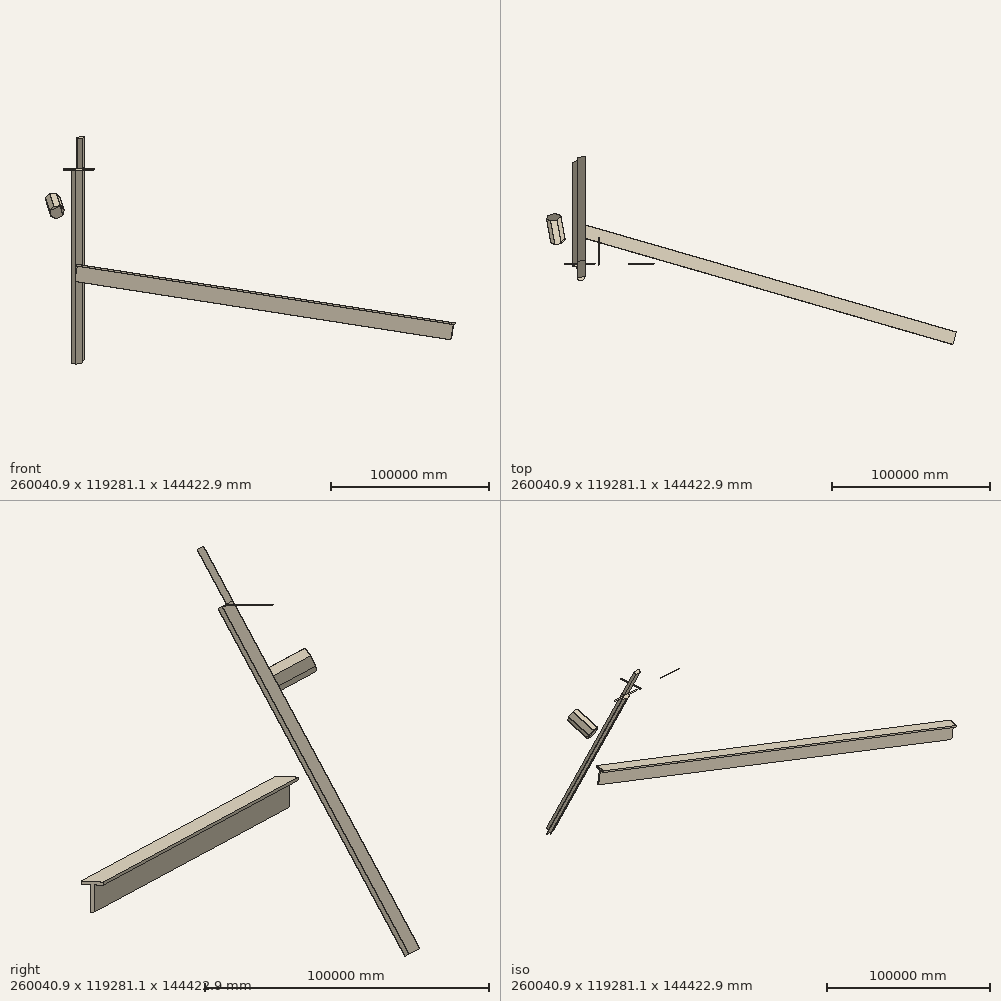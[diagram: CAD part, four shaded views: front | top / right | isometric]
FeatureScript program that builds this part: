
annotation { "Feature Type Name" : "Feature", "Feature Type Description" : "" }
export const myFeature = defineFeature(function(context is Context, id is Id, definition is map)
    precondition{}
    {
        {
            var Q0;
            Q0=qCreatedBy(makeId("Right.planeOp"),FACE);
            var sketch = newSketch(context, id + "F0", { "sketchPlane" : qUnion([Q0])});
            skLineSegment(sketch, "E0", {"start": v(0, 0) * mm, "end": v(0, 75.63) * mm});
            skLineSegment(sketch, "E1", {"start": v(76.11, 75.63) * mm, "end": v(76.11, 0) * mm});
            skLineSegment(sketch, "E2", {"start": v(76.11, 0) * mm, "end": v(0, 0) * mm});
            skLineSegment(sketch, "E3", {"start": v(0, 75.63) * mm, "end": v(76.11, 75.63) * mm});
            skSolve(sketch);
        }
        {
            var Q0;
            Q0=makeQuery(id+"F0.imprint","IMPRINT",FACE,{"disambiguationData":[TD([[makeQuery(id+"F0.imprint","IMPRINT",EDGE,{"derivedFrom":sQuery(id+"F0.wireOp",EDGE,"E0")}),-1.0]])]});
            extrude(context, id + "F1", {"entities" : qUnion([Q0]), "depth" : 1752.6 * mm, "hasSecondDirection" : true, "secondDirectionOppositeDirection" : true, "secondDirectionDepth" : 1752.6 * mm});
        }
        {
            var Q0;
            Q0=makeQuery(id+"F1.opExtrude","CAP_FACE",FACE,{"disambiguationData":[OSD([sQuery(id+"F0.wireOp",EDGE,"E0"),sQuery(id+"F0.wireOp",EDGE,"E1"),sQuery(id+"F0.wireOp",EDGE,"E2"),sQuery(id+"F0.wireOp",EDGE,"E3")])],"isStart":false});
            var sketch = newSketch(context, id + "F2", { "sketchPlane" : qUnion([Q0])});
            skLineSegment(sketch, "E4", {"start": v(38.06, 75.63) * mm, "end": v(38.06, 37.81) * mm});
            skPoint(sketch, "E4.endSnap0", {"position": v(76.11, 37.81) * mm});
            skLineSegment(sketch, "E5", {"start": v(76.11, 37.81) * mm, "end": v(38.06, 37.81) * mm});
            skLineSegment(sketch, "E6", {"start": v(76.11, 75.63) * mm, "end": v(38.06, 75.63) * mm});
            skSolve(sketch);
        }
        {
            var Q0;
            Q0=makeQuery(id+"F2.imprint","IMPRINT",FACE,{"disambiguationData":[TD([[makeQuery(id+"F2.imprint","IMPRINT",EDGE,{"derivedFrom":sQuery(id+"F2.wireOp",EDGE,"E4")}),1.0]])]});
            extrude(context, id + "F3", {"entities" : qUnion([Q0]), "operationType" : NewBodyOperationType.ADD, "depth" : 17399 * mm});
        }
        {
            var Q0;
            Q0=makeQuery(id+"F3.opExtrude","CAP_FACE",FACE,{"disambiguationData":[OSD([sQuery(id+"F0.wireOp",EDGE,"E1"),sQuery(id+"F2.wireOp",EDGE,"E4"),sQuery(id+"F2.wireOp",EDGE,"E5"),sQuery(id+"F2.wireOp",EDGE,"E6")])],"isStart":false});
            var sketch = newSketch(context, id + "F4", { "sketchPlane" : qUnion([Q0])});
            skLineSegment(sketch, "E7", {"start": v(56.95, 109.95) * mm, "end": v(38.06, 75.63) * mm});
            skLineSegment(sketch, "E8", {"start": v(97.56, 110.3) * mm, "end": v(56.95, 109.95) * mm});
            skLineSegment(sketch, "E9", {"start": v(76.11, 37.81) * mm, "end": v(145.73, 33.55) * mm});
            skLineSegment(sketch, "E10", {"start": v(131.28, 84.14) * mm, "end": v(145.73, 33.55) * mm});
            skLineSegment(sketch, "E11", {"start": v(170.17, 109.95) * mm, "end": v(131.28, 84.14) * mm});
            skLineSegment(sketch, "E12", {"start": v(160.88, 120.61) * mm, "end": v(170.17, 109.95) * mm});
            skLineSegment(sketch, "E13", {"start": v(97.56, 110.3) * mm, "end": v(160.88, 120.61) * mm});
            skSolve(sketch);
        }
        {
            var Q0;
            Q0=makeQuery(id+"F4.imprint","IMPRINT",FACE,{"disambiguationData":[TD([[makeQuery(id+"F4.imprint","IMPRINT",EDGE,{"derivedFrom":sQuery(id+"F4.wireOp",EDGE,"E7")}),1.0]])]});
            extrude(context, id + "F5", {"entities" : qUnion([Q0]), "depth" : 16916.4 * mm});
        }
        {
            var Q0;
            {var subQ0=sQuery(id+"F0.wireOp",EDGE,"E1");Q0=makeQuery(id+"F3.boolean.opBoolean","MERGE",FACE,{"derivedFrom":[makeQuery(id+"F1.opExtrude","SWEPT_FACE",FACE,{"disambiguationData":[OSD([subQ0])]}),makeQuery(id+"F3.opExtrude","SWEPT_FACE",FACE,{"disambiguationData":[OSD([subQ0])]})]});}
            var sketch = newSketch(context, id + "F6", { "sketchPlane" : qUnion([Q0])});
            skCircle(sketch, "E14", {"center": v(-926.87, 37.27) * mm, "radius": 301.74 * mm});
            skSolve(sketch);
        }
        {
            var Q0;
            {var subQ0=sQuery(id+"F6.wireOp",EDGE,"E14");var subQ1=sQuery(id+"F0.wireOp",EDGE,"E1");var subQ2=makeQuery(id+"F3.boolean.opBoolean","MERGE",EDGE,{"derivedFrom":[makeQuery(id+"F1.opExtrude","SWEPT_EDGE",EDGE,{"disambiguationData":[OSD([subQ1,sQuery(id+"F0.wireOp",EDGE,"E3")])]}),makeQuery(id+"F3.opExtrude","SWEPT_EDGE",EDGE,{"disambiguationData":[OSD([subQ1,sQuery(id+"F2.wireOp",EDGE,"E6")])]})]});var subQ3=makeQuery(id+"F6.imprint","INTERSECT",VERTEX,{"disambiguationData":[OD(0.0)],"derivedFrom":[subQ2,subQ0]});Q0=makeQuery(id+"F6.imprint","IMPRINT",FACE,{"disambiguationData":[TD([[makeQuery(id+"F6.imprint","IMPRINT",EDGE,{"disambiguationData":[TD([[subQ3,1.0]])],"derivedFrom":subQ0}),1.0]])]});}
            extrude(context, id + "F7", {"entities" : qUnion([Q0]), "depth" : 16611.6 * mm});
        }
        {
            var Q0;
            {var subQ0=sQuery(id+"F6.wireOp",EDGE,"E14");var subQ1=makeQuery(id+"F1.opExtrude","SWEPT_EDGE",EDGE,{"disambiguationData":[OSD([sQuery(id+"F0.wireOp",EDGE,"E1"),sQuery(id+"F0.wireOp",EDGE,"E2")])]});var subQ2=makeQuery(id+"F6.imprint","INTERSECT",VERTEX,{"disambiguationData":[OD(0.0)],"derivedFrom":[subQ1,subQ0]});Q0=makeQuery(id+"F6.imprint","IMPRINT",FACE,{"disambiguationData":[TD([[makeQuery(id+"F6.imprint","IMPRINT",EDGE,{"disambiguationData":[TD([[subQ2,-1.0]])],"derivedFrom":subQ0}),1.0]])]});}
            extrude(context, id + "F8", {"entities" : qUnion([Q0]), "operationType" : NewBodyOperationType.ADD, "depth" : -863.6 * mm});
        }
        {
            var Q0;
            Q0=makeQuery(id+"F1.opExtrude","CAP_FACE",FACE,{"disambiguationData":[OSD([sQuery(id+"F0.wireOp",EDGE,"E0"),sQuery(id+"F0.wireOp",EDGE,"E1"),sQuery(id+"F0.wireOp",EDGE,"E2"),sQuery(id+"F0.wireOp",EDGE,"E3")])],"isStart":true});
            var sketch = newSketch(context, id + "F9", { "sketchPlane" : qUnion([Q0])});
            skCircle(sketch, "E15.cCircle", {"center": v(-38.06, 75.63) * mm, "radius": 238.74 * mm, "construction": true});
            skLineSegment(sketch, "E15.0", {"start": v(439.2, 90.05) * mm, "end": v(-264.2, -344.9) * mm});
            skLineSegment(sketch, "E15.1", {"start": v(-264.2, -344.9) * mm, "end": v(-289.18, 481.73) * mm});
            skLineSegment(sketch, "E15.2", {"start": v(-289.18, 481.73) * mm, "end": v(439.2, 90.05) * mm});
            skPoint(sketch, "E15.0.midPoint", {"position": v(87.5, -127.42) * mm});
            skSolve(sketch);
        }
        {
            var Q0;
            Q0=makeQuery(id+"F9.imprint","IMPRINT",FACE,{"disambiguationData":[TD([[makeQuery(id+"F9.imprint","IMPRINT",EDGE,{"derivedFrom":sQuery(id+"F9.wireOp",EDGE,"E15.0")}),-1.0]])]});
            extrude(context, id + "F10", {"entities" : qUnion([Q0]), "depth" : 19735.8 * mm});
        }
        {
            var Q0;
            Q0=makeQuery(id+"F10.opExtrude","SWEPT_FACE",FACE,{"disambiguationData":[OSD([sQuery(id+"F9.wireOp",EDGE,"E15.2")])]});
            var sketch = newSketch(context, id + "F11", { "sketchPlane" : qUnion([Q0])});
            skLineSegment(sketch, "E16", {"start": v(-12583.52, 482.84) * mm, "end": v(-12931.17, 2228.57) * mm});
            skLineSegment(sketch, "E17", {"start": v(-12931.17, 2228.57) * mm, "end": v(-8013.43, 3020.24) * mm});
            skLineSegment(sketch, "E18", {"start": v(-8013.43, 3020.24) * mm, "end": v(-9408.31, -1238.1) * mm});
            skLineSegment(sketch, "E19", {"start": v(-9408.31, -1238.1) * mm, "end": v(-13769.17, -2878.8) * mm});
            skLineSegment(sketch, "E20", {"start": v(-11972.44, -1560.1) * mm, "end": v(-13769.17, -2878.8) * mm});
            skLineSegment(sketch, "E21", {"start": v(-11972.44, -1560.1) * mm, "end": v(-16336.36, -1767.9) * mm});
            skLineSegment(sketch, "E22", {"start": v(-12583.52, 482.84) * mm, "end": v(-16336.36, -1767.9) * mm});
            skSolve(sketch);
        }
        {
            var Q0;
            {var subQ0=sQuery(id+"F11.wireOp",EDGE,"E16");Q0=makeQuery(id+"F11.imprint","IMPRINT",FACE,{"disambiguationData":[TD([[makeQuery(id+"F11.imprint","IMPRINT",EDGE,{"derivedFrom":subQ0}),-1.0]])]});}
            extrude(context, id + "F12", {"entities" : qUnion([Q0]), "depth" : 21793.2 * mm});
        }
        {
            var Q0;
            Q0 = qSketchRegion(id + "F11", true);
            extrude(context, id + "F13", {"entities" : qUnion([Q0]), "depth" : -139014.2 * mm});
        }
        {
            var Q0;
            Q0=makeQuery(id+"F13.opExtrude","SWEPT_FACE",FACE,{"disambiguationData":[OSD([sQuery(id+"F11.wireOp",EDGE,"E18")])]});
            var sketch = newSketch(context, id + "F14", { "sketchPlane" : qUnion([Q0])});
            skText(sketch, "E23", { "text": "T", "fontName": "OpenSans-Regular.ttf"});
            const initialGuessF14  = {"E23": [15.99303, -72.28626, 1, 0, 11.0518]};
            skSetInitialGuess(sketch, initialGuessF14);
            skSolve(sketch);
        }
        {
            var Q0;
            Q0 = qSketchRegion(id + "F14", true);
            extrude(context, id + "F15", {"entities" : qUnion([Q0]), "depth" : 250850.4 * mm});
        }
        {
            var Q0;
            Q0=makeQuery(id+"F13.opExtrude","SWEPT_FACE",FACE,{"disambiguationData":[OSD([sQuery(id+"F11.wireOp",EDGE,"E17")])]});
            var sketch = newSketch(context, id + "F16", { "sketchPlane" : qUnion([Q0])});
            skCircle(sketch, "E24.cCircle", {"center": v(24901.09, -30753.93) * mm, "radius": 4788.8 * mm, "construction": true});
            skLineSegment(sketch, "E24.0", {"start": v(21201.47, -33794.57) * mm, "end": v(20217.15, -29757.27) * mm});
            skLineSegment(sketch, "E24.1", {"start": v(20217.15, -29757.27) * mm, "end": v(22759.92, -26470.47) * mm});
            skLineSegment(sketch, "E24.2", {"start": v(22759.92, -26470.47) * mm, "end": v(26915.04, -26409.2) * mm});
            skLineSegment(sketch, "E24.3", {"start": v(26915.04, -26409.2) * mm, "end": v(29553.6, -29619.62) * mm});
            skLineSegment(sketch, "E24.4", {"start": v(29553.6, -29619.62) * mm, "end": v(28688.73, -33684.19) * mm});
            skLineSegment(sketch, "E24.5", {"start": v(28688.73, -33684.19) * mm, "end": v(24971.68, -35542.22) * mm});
            skLineSegment(sketch, "E24.6", {"start": v(24971.68, -35542.22) * mm, "end": v(21201.47, -33794.57) * mm});
            skSolve(sketch);
        }
        {
            var Q0;
            Q0=makeQuery(id+"F16.imprint","IMPRINT",FACE,{"disambiguationData":[TD([[makeQuery(id+"F16.imprint","IMPRINT",EDGE,{"derivedFrom":sQuery(id+"F16.wireOp",EDGE,"E24.0")}),-1.0]])]});
            extrude(context, id + "F17", {"entities" : qUnion([Q0]), "depth" : 1346.2 * mm});
        }
        {
            var Q0;
            Q0=makeQuery(id+"F16.imprint","IMPRINT",FACE,{"disambiguationData":[TD([[makeQuery(id+"F16.imprint","IMPRINT",EDGE,{"derivedFrom":sQuery(id+"F16.wireOp",EDGE,"E24.0")}),-1.0]])]});
            extrude(context, id + "F18", {"entities" : qUnion([Q0]), "depth" : 17221.2 * mm});
        }
    });
